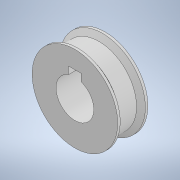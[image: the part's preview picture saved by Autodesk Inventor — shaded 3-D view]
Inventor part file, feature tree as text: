
AUTODESK INVENTOR PART (.ipt)
format: ipt  version: 2022 (Build 260153000, 153)  size: 136,192 bytes
history: native  units: mm
features: sketch x2, extrude x1, revolve x1, projected_geometry x1
ambient origin geometry x8: Origin, YZ Plane, XZ Plane, XY Plane, X Axis, Y Axis, Z Axis, Center Point
bodies: Body1 (feature_tree)
feature tree (5):
  extrude  "Extrusion3"  Depth=5.0mm
  sketch  "Sketch5"  dims[d19=5.0mm d20=30.0mm d21=12.0mm d22=0.0mm d23=7.0mm d24=2.0mm d25=1.0mm d26=1.0mm d28=90.0deg]
  revolve  "Revolution1"  [1 undecoded]
  sketch  "Sketch4"  dims[d17=15.0mm d18=5.0mm]
  projected_geometry  "Projected Loop3"
note: 1 required parameter value undecoded (feature->parameter linkage not recoverable at this tier; creation-order binding heuristic only, values carry confidence <= 0.55)
